# Revit family: Puerta entrada HOBBIT
name_source: partatom
category: Puertas
revit_build: Autodesk Revit 2016 (Build: 20150714_1515(x64)
units: mm (PartAtom-declared; Revit-internal decimal feet)

## family parameters
Anfitrión = Muro
Compartido = No
Corte con vacíos al cargar = No
Número OmniClass = 23.30.10.00
Punto de cálculo de habitación = No
Siempre vertical = Sí
Título OmniClass = Doors

## types (1)
- Puerta entrada HOBBIT
    Altura = 3000 mm
    Anchura = 1000 mm
    Anchura de marco = 75 mm  [stored 0.246063 ft]
    Cierre de muro = Por anfitrión
    Función = Interior
    LADRILLO-material = <Por categoría>
    MARCO-linea exterior = 3000 mm
    MARCO-linea interior = 2800 mm
    MARCO-material = <Por categoría>
    Material ladrillo = <Por categoría>
    POMO-altura = 1500 mm
    POMO-material = <Por categoría>
    PUERTA-diametro = 2600 mm
    PUERTA-grosor = 74 mm
    PUERTA-material = <Por categoría>
    PUERTA_mitad de grosor = 37 mm
    Proyección marco ext. = 25 mm  [stored 0.082021 ft]
    Proyección marco int. = 25 mm  [stored 0.082021 ft]

note: [stored X ft] marks values corroborated as IEEE doubles in the binary element streams (Revit-internal decimal feet)
